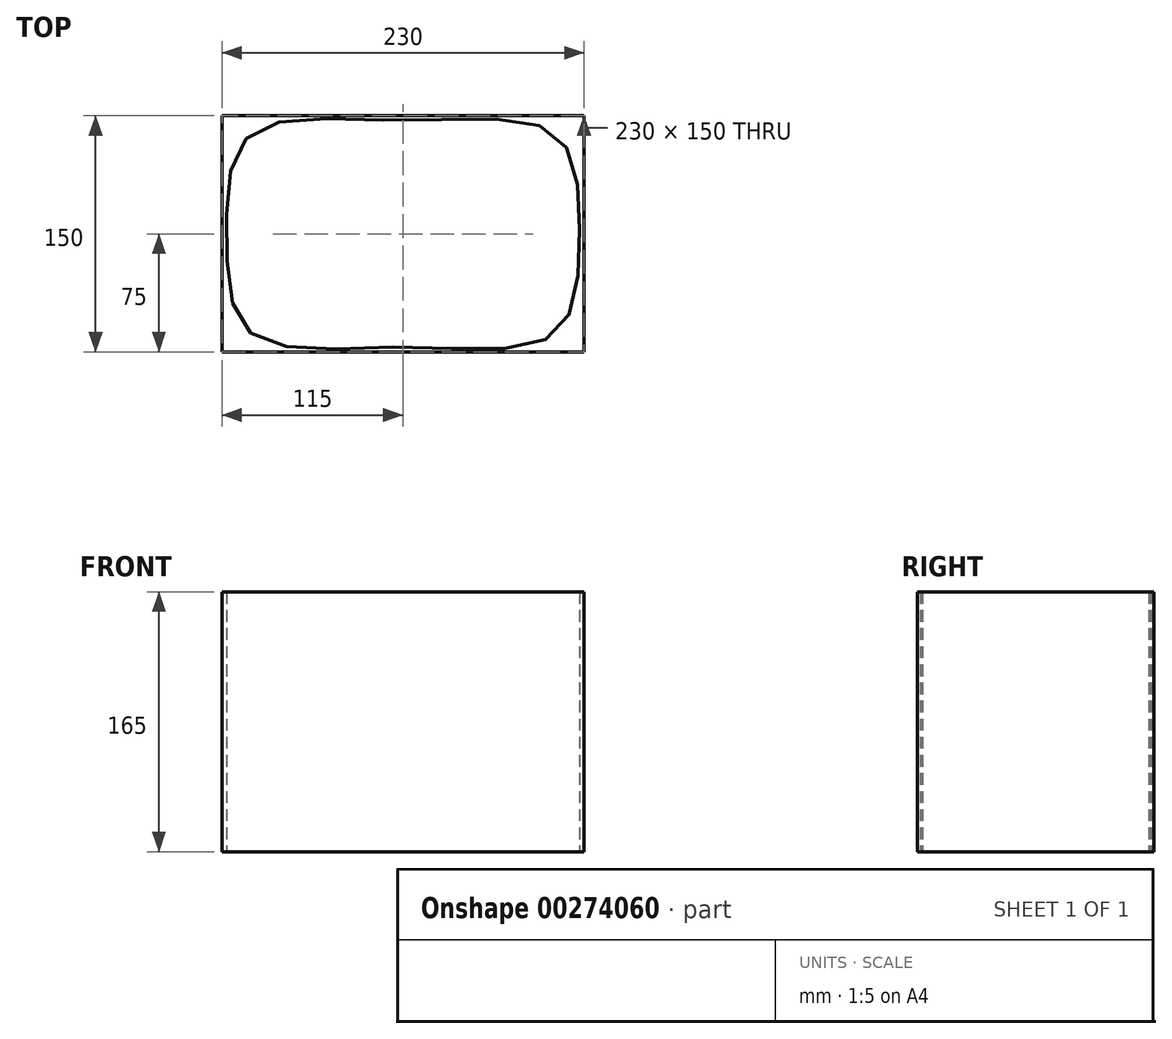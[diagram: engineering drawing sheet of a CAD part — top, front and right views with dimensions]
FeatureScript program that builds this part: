
annotation { "Feature Type Name" : "Feature", "Feature Type Description" : "" }
export const myFeature = defineFeature(function(context is Context, id is Id, definition is map)
    precondition{}
    {
        {
            var Q0;
            Q0=qCreatedBy(makeId("Top.planeOp"),FACE);
            var sketch = newSketch(context, id + "F0", { "sketchPlane" : qUnion([Q0])});
            skLineSegment(sketch, "E0.bottom", {"start": v(115, -75) * mm, "end": v(-115, -75) * mm});
            skLineSegment(sketch, "E0.top", {"start": v(115, 75) * mm, "end": v(-115, 75) * mm});
            skLineSegment(sketch, "E0.left", {"start": v(115, -75) * mm, "end": v(115, 75) * mm});
            skLineSegment(sketch, "E0.right", {"start": v(-115, -75) * mm, "end": v(-115, 75) * mm});
            skPoint(sketch, "E0.middle", {"position": v(0, 0) * mm});
            skLineSegment(sketch, "E1.bottom", {"start": v(-96.77, -63.11) * mm, "end": v(96.77, -63.11) * mm, "construction": true});
            skLineSegment(sketch, "E1.top", {"start": v(-96.77, 63.11) * mm, "end": v(96.77, 63.11) * mm, "construction": true});
            skLineSegment(sketch, "E1.left", {"start": v(-96.77, -63.11) * mm, "end": v(-96.77, 63.11) * mm, "construction": true});
            skLineSegment(sketch, "E1.right", {"start": v(96.77, -63.11) * mm, "end": v(96.77, 63.11) * mm, "construction": true});
            skFitSpline(sketch, "E2", {"points": [v(-96.77, -63.11) * mm, v(0, -72) * mm, v(96.77, -63.11) * mm, v(112, 0) * mm, v(96.77, 63.11) * mm, v(0, 72) * mm, v(-96.77, 63.11) * mm, v(-112, 0) * mm, v(-96.77, -63.11) * mm]});
            skLineSegment(sketch, "E3", {"start": v(-115, -75) * mm, "end": v(0, 0) * mm, "construction": true});
            skLineSegment(sketch, "E4", {"start": v(115, 75) * mm, "end": v(0, 0) * mm, "construction": true});
            skLineSegment(sketch, "E5", {"start": v(-115, 75) * mm, "end": v(0, 0) * mm, "construction": true});
            skLineSegment(sketch, "E6", {"start": v(0, 0) * mm, "end": v(115, -75) * mm, "construction": true});
            skSolve(sketch);
        }
        {
            var Q0;
            Q0 = qSketchRegion(id + "F0", true);
            extrude(context, id + "F1", {"entities" : qUnion([Q0]), "depth" : 165 * mm});
        }
        {
            var Q0;
            Q0=qCreatedBy(makeId("Top.planeOp"),FACE);
            cPlane(context, id + "F2", {"entities" : qUnion([Q0]), "cplaneType" : CPlaneType.OFFSET, "offset" : 4 * mm, "width" : 150 * mm, "height" : 150 * mm});
        }
    });
